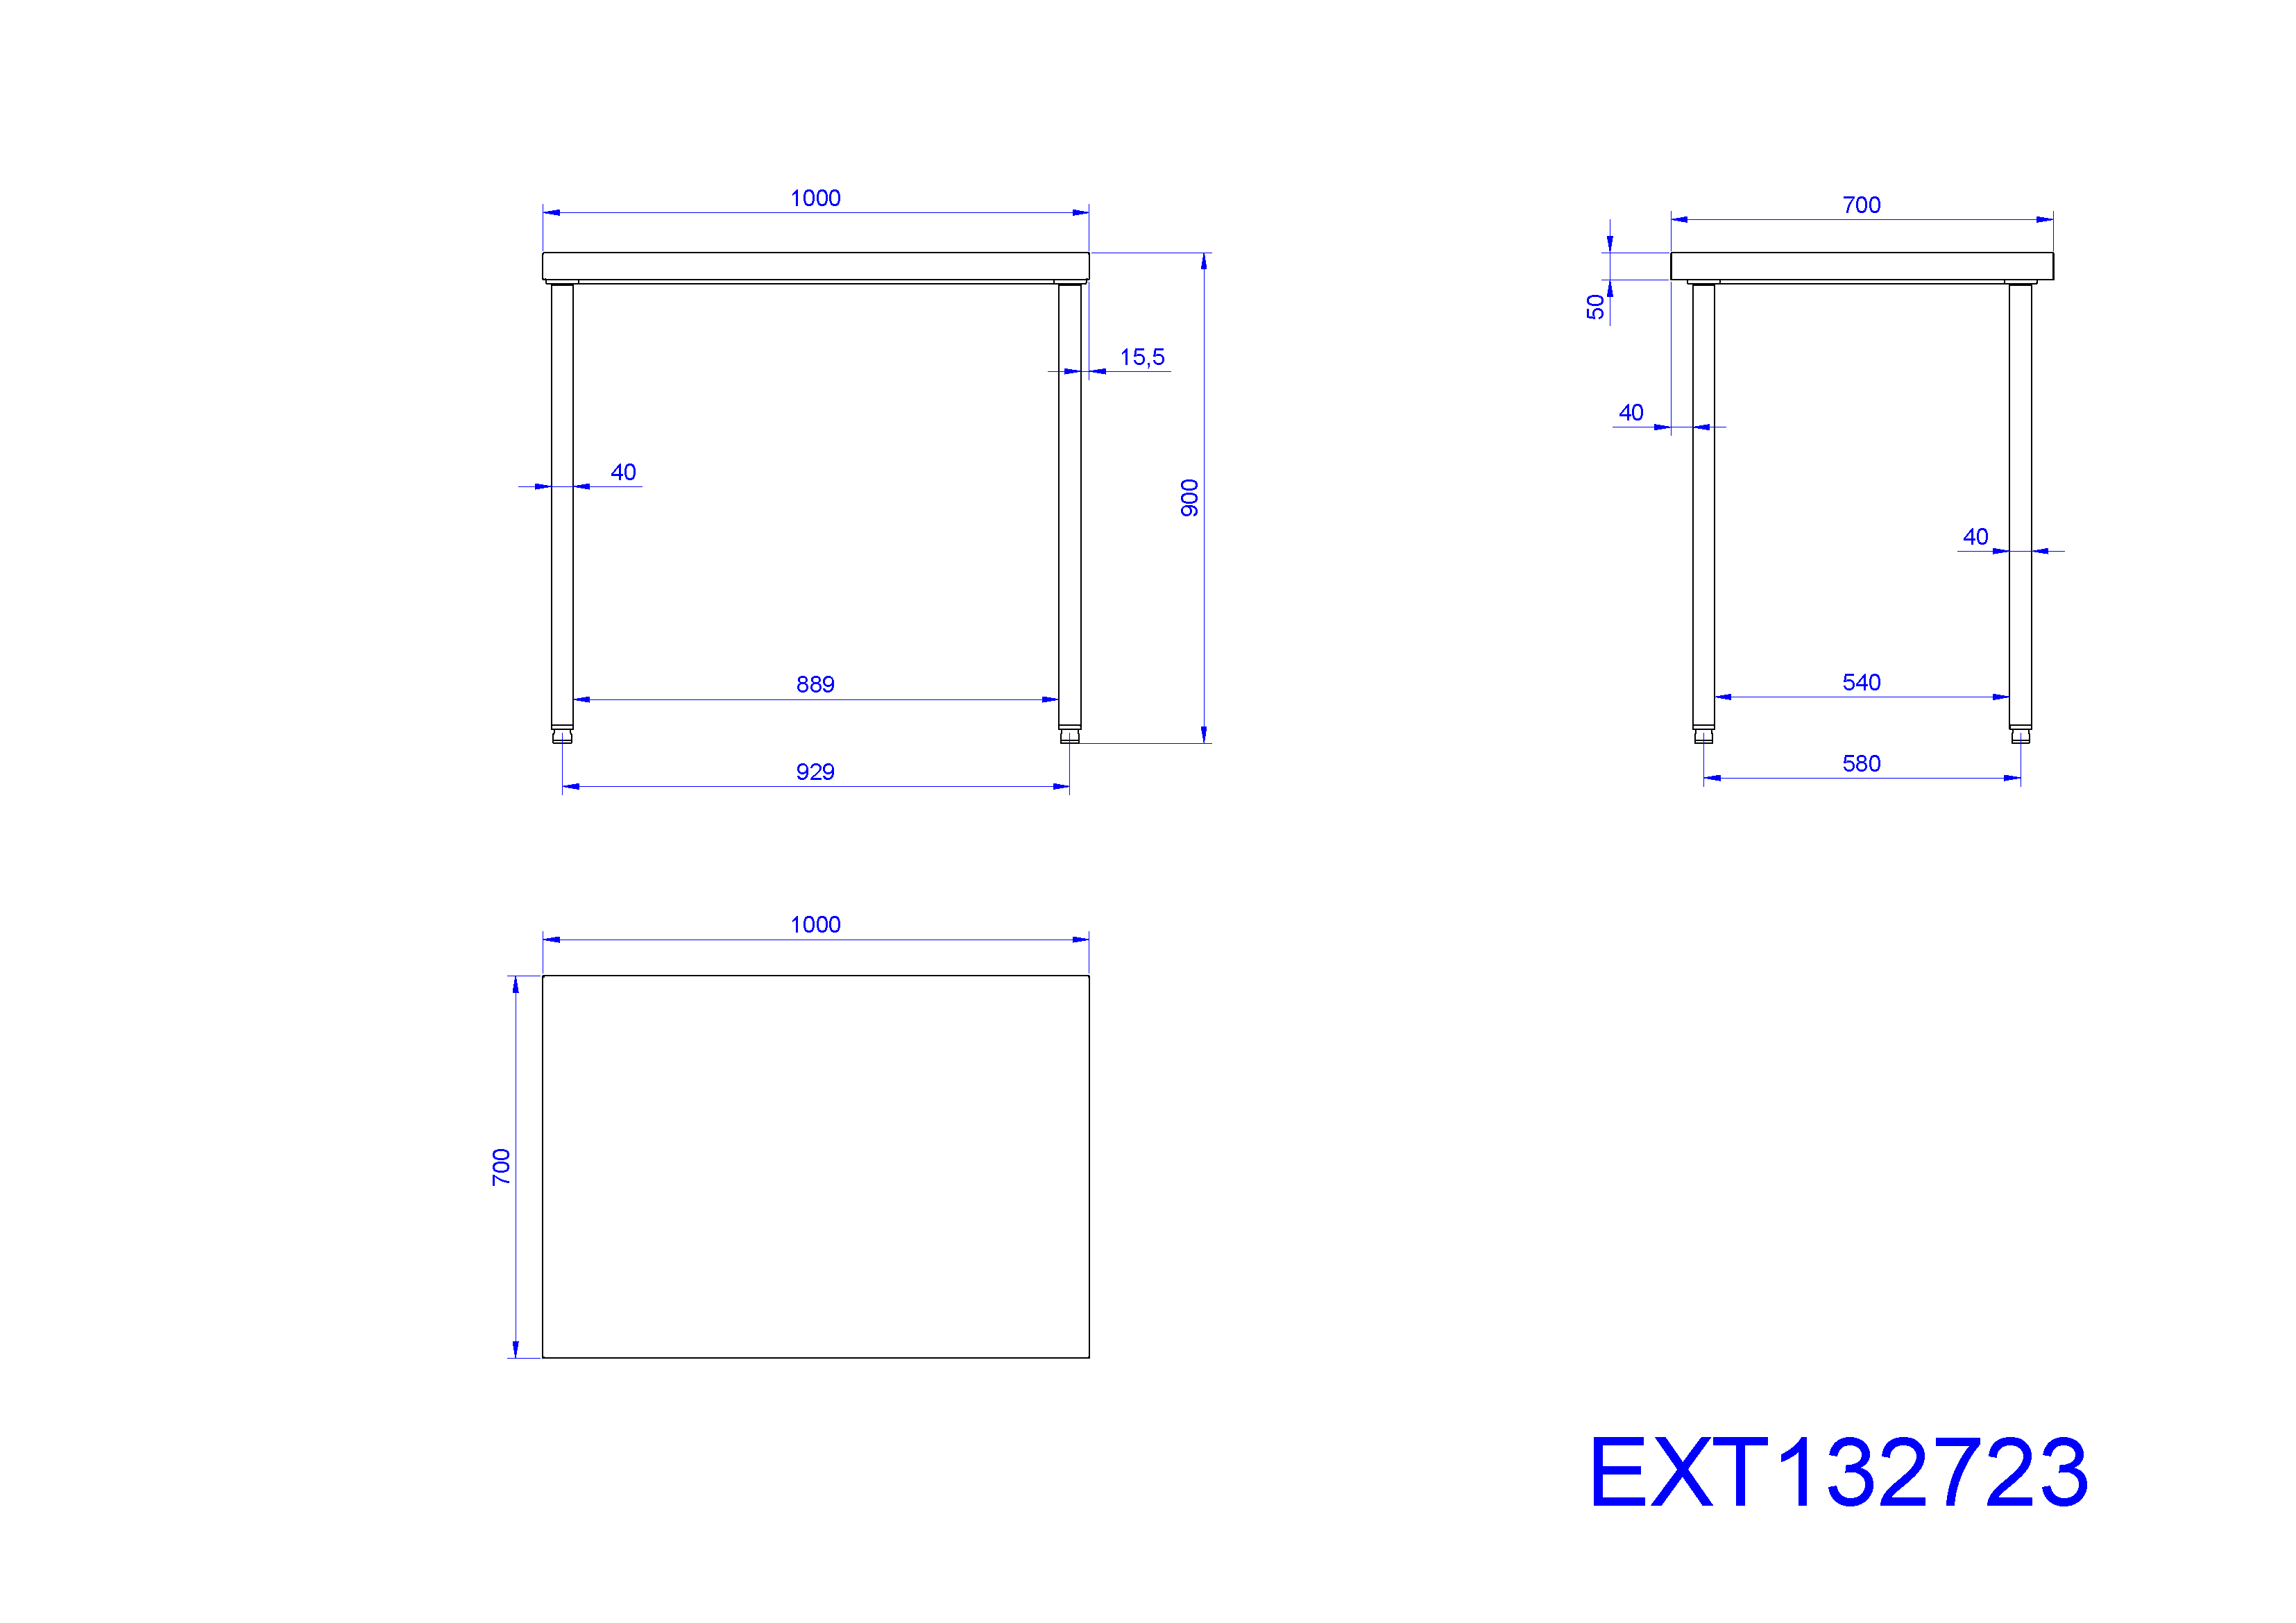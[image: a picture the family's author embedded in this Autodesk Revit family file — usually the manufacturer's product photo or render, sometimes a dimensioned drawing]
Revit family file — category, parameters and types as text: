
# Revit family: QF_ELECTROLUXPROFESSIONAL_132725_TG1400PN
name_source: partatom
category: Attrezzature speciali
units: mm (PartAtom-declared; Revit-internal decimal feet)

## family parameters
Basato su piano di lavoro = No
Condiviso = No
Punto di calcolo locali = No
Quota connettore circolare = Usa diametro
Sempre verticale = Sì
Taglio con vuoti quando caricato = No
Tipo di parte = Normale

## types (1)
- Standard
    Accessory = Sì
    Cold Water Size = 0 mm
    Compressed Air Pressure = 0.0 Pa
    Compressed Air Size = 0 mm
    Compressed Air Volume = 0.0 L/s
    Condensate Return Size = 0 mm
    Cycle = 0 Hz
    Depth Actual = 700 mm  [stored 2.29659 ft]
    Descrizione = WORK TABLE 1400 MM
    Direct Waste Size = 0 mm
    Gas Input Pressure = 0
    Gas KW = 0
    Gas Size = 0 mm
    HP = 0 HP
    Height Actual = 900 mm  [stored 2.95276 ft]
    Hot Water Size = 0 mm
    Item Number = 132725
    Length Actual = 1400 mm  [stored 4.59318 ft]
    Modello = TG1400PN
    Phase = 0
    Produttore = Electrolux Professional
    Prospetto di default = 0 mm  [stored 0 ft]
    Refrigerant Compressor Remote = Sì
    Refrigeration Liquid Line Size = 0 mm  [stored 0 ft]
    Refrigeration Suction Line Size = 0 mm  [stored 0 ft]
    Steam Consumption per Hour = 0
    Steam Supply Maximum Pressure = 0.0 Pa
    Steam Supply Minimum Pressure = 0.0 Pa
    Steam Supply Size = 0 mm
    URL = https://www.electroluxprofessional.com
    URL Manufacturer = https://www.electroluxprofessional.com
    Volts = 0 V
    Watts = 0 W
    Weight = 33.00 kg

note: source unit labels omitted for Gas Input Pressure — the stored unit's dimension contradicts the parameter name (converter mislabeling)

note: [stored X ft] marks values corroborated as IEEE doubles in the binary element streams (Revit-internal decimal feet)

## geometry (parser evidence)
native form markers: Sweep x2
no freeform markers — native parametric forms only
